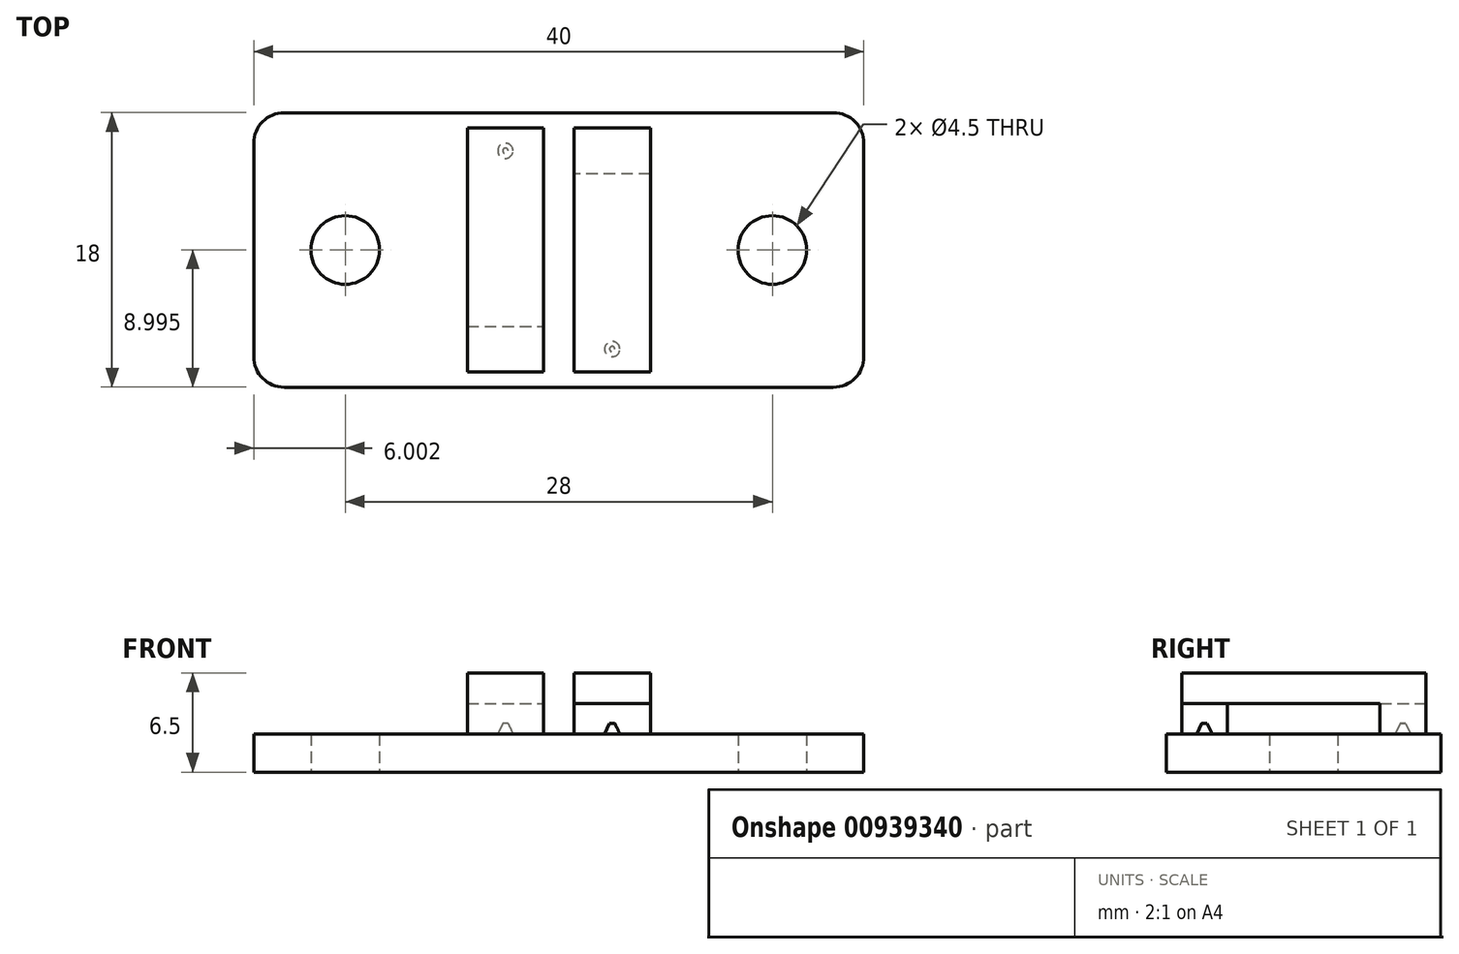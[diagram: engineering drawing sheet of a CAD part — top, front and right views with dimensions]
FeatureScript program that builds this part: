
annotation { "Feature Type Name" : "Feature", "Feature Type Description" : "" }
export const myFeature = defineFeature(function(context is Context, id is Id, definition is map)
    precondition{}
    {
        {
            var Q0;
            Q0=qCreatedBy(makeId("Top.planeOp"),FACE);
            var sketch = newSketch(context, id + "F0", { "sketchPlane" : qUnion([Q0])});
            skLineSegment(sketch, "E0.bottom", {"start": v(-18.19, 10.57) * mm, "end": v(17.81, 10.57) * mm});
            skLineSegment(sketch, "E0.top", {"start": v(-18.19, -7.43) * mm, "end": v(17.81, -7.43) * mm});
            skLineSegment(sketch, "E0.left", {"start": v(-20.19, 8.57) * mm, "end": v(-20.19, -5.43) * mm});
            skLineSegment(sketch, "E0.right", {"start": v(19.81, 8.57) * mm, "end": v(19.81, -5.43) * mm});
            skLineSegment(sketch, "E1", {"start": v(-20.19, 1.57) * mm, "end": v(19.81, 1.57) * mm, "construction": true});
            skCircle(sketch, "E2", {"center": v(13.81, 1.57) * mm, "radius": 2.25 * mm});
            skCircle(sketch, "E3", {"center": v(-14.19, 1.57) * mm, "radius": 2.25 * mm});
            skPoint(sketch, "E4.visualSharp", {"position": v(-20.19, -7.43) * mm});
            skArc(sketch, "E4.filletArc", {"start": v(-20.19, -5.43) * mm, "mid": v(-19.6, -6.85) * mm, "end": v(-18.19, -7.43) * mm});
            skPoint(sketch, "E5.visualSharp", {"position": v(-20.19, 10.57) * mm});
            skArc(sketch, "E5.filletArc", {"start": v(-18.19, 10.57) * mm, "mid": v(-19.6, 9.98) * mm, "end": v(-20.19, 8.57) * mm});
            skPoint(sketch, "E6.visualSharp", {"position": v(19.81, -7.43) * mm});
            skArc(sketch, "E6.filletArc", {"start": v(17.81, -7.43) * mm, "mid": v(19.23, -6.85) * mm, "end": v(19.81, -5.43) * mm});
            skPoint(sketch, "E7.visualSharp", {"position": v(19.81, 10.57) * mm});
            skArc(sketch, "E7.filletArc", {"start": v(19.81, 8.57) * mm, "mid": v(19.23, 9.98) * mm, "end": v(17.81, 10.57) * mm});
            skSolve(sketch);
        }
        {
            var Q0;
            Q0=makeQuery(id+"F0.imprint","IMPRINT",FACE,{"disambiguationData":[TD([[makeQuery(id+"F0.imprint","IMPRINT",EDGE,{"derivedFrom":sQuery(id+"F0.wireOp",EDGE,"E0.bottom")}),-1.0]])]});
            extrude(context, id + "F1", {"entities" : qUnion([Q0]), "depth" : 2.5 * mm, "offsetDistance" : 25 * mm});
        }
        {
            var Q0;
            Q0=makeQuery(id+"F1.opExtrude","CAP_FACE",FACE,{"disambiguationData":[OSD([sQuery(id+"F0.wireOp",EDGE,"E0.bottom"),sQuery(id+"F0.wireOp",EDGE,"E0.top"),sQuery(id+"F0.wireOp",EDGE,"E0.left"),sQuery(id+"F0.wireOp",EDGE,"E0.right"),sQuery(id+"F0.wireOp",EDGE,"E2"),sQuery(id+"F0.wireOp",EDGE,"E3")])],"isStart":false});
            var sketch = newSketch(context, id + "F2", { "sketchPlane" : qUnion([Q0])});
            skLineSegment(sketch, "E8.bottom", {"start": v(-6.19, -3.43) * mm, "end": v(-1.19, -3.43) * mm});
            skLineSegment(sketch, "E8.top", {"start": v(-6.19, -6.43) * mm, "end": v(-1.19, -6.43) * mm});
            skLineSegment(sketch, "E8.left", {"start": v(-6.19, -3.43) * mm, "end": v(-6.19, -6.43) * mm});
            skLineSegment(sketch, "E8.right", {"start": v(-1.19, -3.43) * mm, "end": v(-1.19, -6.43) * mm});
            skCircle(sketch, "E9.1", {"center": v(-14.19, 1.57) * mm, "radius": 2.25 * mm});
            skCircle(sketch, "E9.2", {"center": v(13.81, 1.57) * mm, "radius": 2.25 * mm});
            skLineSegment(sketch, "E10", {"start": v(-20.19, 1.57) * mm, "end": v(19.81, 1.57) * mm, "construction": true});
            skLineSegment(sketch, "E11", {"start": v(-0.19, 10.57) * mm, "end": v(-0.19, -7.43) * mm, "construction": true});
            skLineSegment(sketch, "E12.1.0", {"start": v(0.81, 6.57) * mm, "end": v(0.81, 9.57) * mm});
            skLineSegment(sketch, "E12.1.1", {"start": v(5.81, 9.57) * mm, "end": v(0.81, 9.57) * mm});
            skLineSegment(sketch, "E12.1.2", {"start": v(5.81, 6.57) * mm, "end": v(5.81, 9.57) * mm});
            skLineSegment(sketch, "E12.1.3", {"start": v(5.81, 6.57) * mm, "end": v(0.81, 6.57) * mm});
            skPoint(sketch, "E12.center", {"position": v(-0.19, 1.57) * mm});
            skCircle(sketch, "E13", {"center": v(3.31, -4.93) * mm, "radius": 0.5 * mm});
            skPoint(sketch, "E13.centerSnap0", {"position": v(3.31, 6.57) * mm});
            skPoint(sketch, "E13.centerSnap1", {"position": v(-1.19, -4.93) * mm});
            skCircle(sketch, "E14.1.0", {"center": v(-3.69, 8.07) * mm, "radius": 0.5 * mm});
            skSolve(sketch);
        }
        {
            var Q0;
            Q0=makeQuery(id+"F2.imprint","IMPRINT",FACE,{"disambiguationData":[TD([[makeQuery(id+"F2.imprint","IMPRINT",EDGE,{"derivedFrom":sQuery(id+"F2.wireOp",EDGE,"E8.bottom")}),-1.0]])]});
            var Q1;
            Q1=makeQuery(id+"F2.imprint","IMPRINT",FACE,{"disambiguationData":[TD([[makeQuery(id+"F2.imprint","IMPRINT",EDGE,{"derivedFrom":sQuery(id+"F2.wireOp",EDGE,"E12.1.0")}),-1.0]])]});
            extrude(context, id + "F3", {"entities" : qUnion([Q0, Q1]), "operationType" : NewBodyOperationType.ADD, "depth" : 2 * mm, "offsetDistance" : 25 * mm});
        }
        {
            var Q0;
            Q0=makeQuery(id+"F3.opExtrude","CAP_FACE",FACE,{"disambiguationData":[OSD([sQuery(id+"F2.wireOp",EDGE,"E8.bottom"),sQuery(id+"F2.wireOp",EDGE,"E8.top"),sQuery(id+"F2.wireOp",EDGE,"E8.left"),sQuery(id+"F2.wireOp",EDGE,"E8.right")])],"isStart":false});
            var sketch = newSketch(context, id + "F4", { "sketchPlane" : qUnion([Q0])});
            skPoint(sketch, "E15.0", {"position": v(0.81, 9.57) * mm});
            skLineSegment(sketch, "E16.bottom", {"start": v(-6.19, -6.43) * mm, "end": v(-1.19, -6.43) * mm});
            skLineSegment(sketch, "E16.top", {"start": v(-6.19, 9.57) * mm, "end": v(-1.19, 9.57) * mm});
            skLineSegment(sketch, "E16.left", {"start": v(-6.19, -6.43) * mm, "end": v(-6.19, 9.57) * mm});
            skLineSegment(sketch, "E16.right", {"start": v(-1.19, -6.43) * mm, "end": v(-1.19, 9.57) * mm});
            skPoint(sketch, "E17.0", {"position": v(5.81, 9.57) * mm});
            skLineSegment(sketch, "E18.bottom", {"start": v(5.81, 9.57) * mm, "end": v(0.81, 9.57) * mm});
            skLineSegment(sketch, "E18.top", {"start": v(5.81, -6.43) * mm, "end": v(0.81, -6.43) * mm});
            skLineSegment(sketch, "E18.left", {"start": v(5.81, 9.57) * mm, "end": v(5.81, -6.43) * mm});
            skLineSegment(sketch, "E18.right", {"start": v(0.81, 9.57) * mm, "end": v(0.81, -6.43) * mm});
            skSolve(sketch);
        }
        {
            var Q0;
            {var subQ0=sQuery(id+"F4.wireOp",EDGE,"E16.top");Q0=makeQuery(id+"F4.imprint","IMPRINT",FACE,{"disambiguationData":[TD([[makeQuery(id+"F4.imprint","IMPRINT",EDGE,{"derivedFrom":subQ0}),-1.0]])]});}
            var Q1;
            Q1=makeQuery(id+"F4.imprint","IMPRINT",FACE,{"disambiguationData":[TD([[makeQuery(id+"F4.imprint","IMPRINT",EDGE,{"derivedFrom":sQuery(id+"F4.wireOp",EDGE,"E18.bottom")}),1.0]])]});
            var Q2;
            {var subQ0=sQuery(id+"F4.wireOp",EDGE,"E16.bottom");Q2=makeQuery(id+"F4.imprint","IMPRINT",FACE,{"disambiguationData":[TD([[makeQuery(id+"F4.imprint","IMPRINT",EDGE,{"derivedFrom":subQ0}),1.0]])]});}
            extrude(context, id + "F5", {"entities" : qUnion([Q0, Q1, Q2]), "operationType" : NewBodyOperationType.ADD, "depth" : 2 * mm, "offsetDistance" : 25 * mm});
        }
        {
            var Q0;
            Q0=makeQuery(id+"F2.imprint","IMPRINT",FACE,{"disambiguationData":[TD([[makeQuery(id+"F2.imprint","IMPRINT",EDGE,{"derivedFrom":sQuery(id+"F2.wireOp",EDGE,"E14.1.0")}),1.0]])]});
            var Q1;
            Q1=makeQuery(id+"F2.imprint","IMPRINT",FACE,{"disambiguationData":[TD([[makeQuery(id+"F2.imprint","IMPRINT",EDGE,{"derivedFrom":sQuery(id+"F2.wireOp",EDGE,"E13")}),1.0]])]});
            extrude(context, id + "F6", {"entities" : qUnion([Q0, Q1]), "operationType" : NewBodyOperationType.ADD, "depth" : 0.7 * mm, "offsetDistance" : 25 * mm, "hasDraft" : true, "draftAngle" : 25 * degree, "draftPullDirection" : true});
        }
    });
